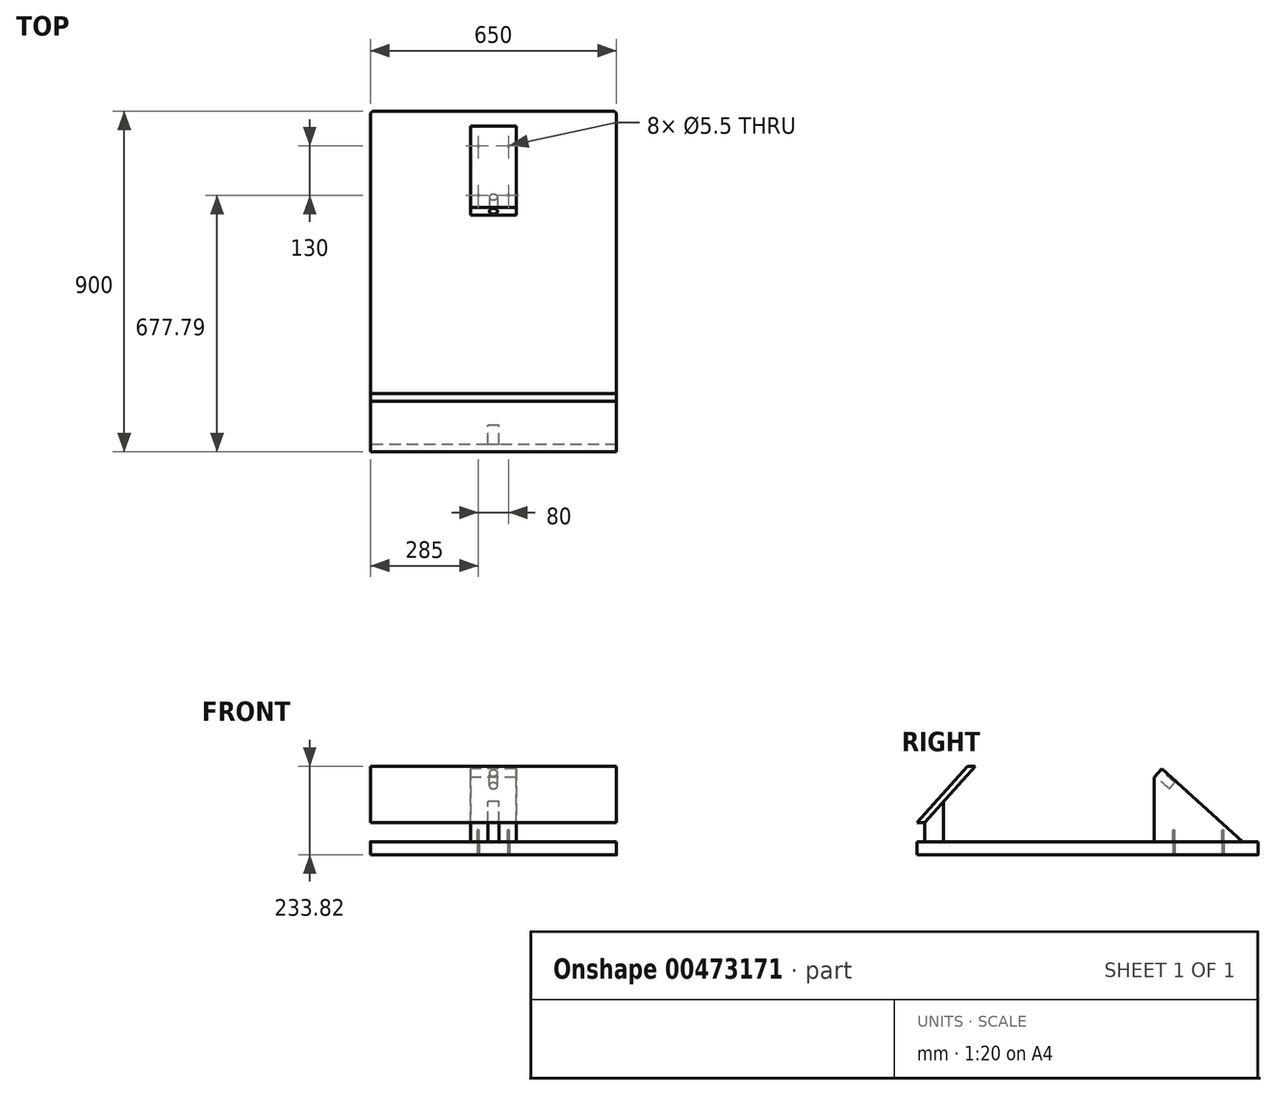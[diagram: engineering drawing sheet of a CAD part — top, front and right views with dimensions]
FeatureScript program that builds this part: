
annotation { "Feature Type Name" : "Feature", "Feature Type Description" : "" }
export const myFeature = defineFeature(function(context is Context, id is Id, definition is map)
    precondition{}
    {
        {
            assignVariable(context, id + "F0", {"name" : "Largeur_Base", "anyValue" : 650});
        }
        {
            assignVariable(context, id + "F1", {"name" : "Bitonio", "anyValue" : 15});
        }
        {
            assignVariable(context, id + "F2", {"name" : "Epaisseur_Arc", "anyValue" : getVariable(context, 'Bitonio') * 2});
        }
        {
            var Q0;
            Q0=qCreatedBy(makeId("Right.planeOp"),FACE);
            var sketch = newSketch(context, id + "F3", { "sketchPlane" : qUnion([Q0])});
            skLineSegment(sketch, "E0.bottom", {"start": v(-655.07, 0) * mm, "end": v(244.93, 0) * mm});
            skLineSegment(sketch, "E0.top", {"start": v(-655.07, 35) * mm, "end": v(244.93, 35) * mm});
            skLineSegment(sketch, "E0.left", {"start": v(-655.07, 0) * mm, "end": v(-655.07, 35) * mm});
            skLineSegment(sketch, "E0.right", {"start": v(244.93, 0) * mm, "end": v(244.93, 35) * mm});
            skLineSegment(sketch, "E1.bottom", {"start": v(-655.07, 35) * mm, "end": v(-635.07, 35) * mm});
            skLineSegment(sketch, "E1.top", {"start": v(-655.07, 85) * mm, "end": v(-635.07, 85) * mm});
            skLineSegment(sketch, "E1.left", {"start": v(-655.07, 35) * mm, "end": v(-655.07, 85) * mm});
            skLineSegment(sketch, "E1.right", {"start": v(-635.07, 35) * mm, "end": v(-635.07, 85) * mm});
            skLineSegment(sketch, "E2", {"start": v(-655.07, 85) * mm, "end": v(-521.46, 233.82) * mm});
            skLineSegment(sketch, "E3", {"start": v(-635.07, 85) * mm, "end": v(-501.46, 233.82) * mm});
            skLineSegment(sketch, "E4", {"start": v(-501.46, 233.82) * mm, "end": v(-521.46, 233.82) * mm});
            skLineSegment(sketch, "E5", {"start": v(-585.07, 35) * mm, "end": v(-585.07, 140.7) * mm});
            skLineSegment(sketch, "E6", {"start": v(-29.36, 35) * mm, "end": v(-29.36, 204.9) * mm});
            skLineSegment(sketch, "E7", {"start": v(-29.36, 204.9) * mm, "end": v(-9.32, 227.23) * mm});
            skLineSegment(sketch, "E8", {"start": v(-9.32, 227.23) * mm, "end": v(204.8, 35) * mm});
            skSolve(sketch);
        }
        {
            var Q0;
            Q0=makeQuery(id+"F3.imprint","IMPRINT",FACE,{"disambiguationData":[TD([[makeQuery(id+"F3.imprint","IMPRINT",EDGE,{"derivedFrom":sQuery(id+"F3.wireOp",EDGE,"E0.bottom")}),1.0]])]});
            var Q1;
            Q1=makeQuery(id+"F3.imprint","IMPRINT",FACE,{"disambiguationData":[TD([[makeQuery(id+"F3.imprint","IMPRINT",EDGE,{"derivedFrom":sQuery(id+"F3.wireOp",EDGE,"E1.bottom")}),1.0]])]});
            var Q2;
            {var subQ1=sQuery(id+"F3.wireOp",EDGE,"E1.top");Q2=makeQuery(id+"F3.imprint","IMPRINT",FACE,{"disambiguationData":[TD([[makeQuery(id+"F3.imprint","IMPRINT",EDGE,{"derivedFrom":subQ1}),1.0]])]});}
            extrude(context, id + "F4", {"entities" : qUnion([Q0, Q1, Q2]), "depth" : (getVariable(context, 'Largeur_Base')) * mm, "offsetDistance" : 25 * mm, "symmetric" : true});
        }
        {
            var Q0;
            Q0=makeQuery(id+"F4.opExtrude","CAP_EDGE",EDGE,{"disambiguationData":[OSD([sQuery(id+"F3.wireOp",EDGE,"E0.left"),sQuery(id+"F3.wireOp",EDGE,"E1.left")])],"isStart":false});
            var Q1;
            Q1=makeQuery(id+"F4.opExtrude","CAP_EDGE",EDGE,{"disambiguationData":[OSD([sQuery(id+"F3.wireOp",EDGE,"E0.right")])],"isStart":false});
            var Q2;
            Q2=makeQuery(id+"F4.opExtrude","CAP_EDGE",EDGE,{"disambiguationData":[OSD([sQuery(id+"F3.wireOp",EDGE,"E0.left"),sQuery(id+"F3.wireOp",EDGE,"E1.left")])],"isStart":true});
            var Q3;
            Q3=makeQuery(id+"F4.opExtrude","CAP_EDGE",EDGE,{"disambiguationData":[OSD([sQuery(id+"F3.wireOp",EDGE,"E0.right")])],"isStart":true});
            fillet(context, id + "F5", {"entities" : qUnion([Q0, Q1, Q2, Q3]), "radius" : 10 * mm, "tangentPropagation" : true, "allowEdgeOverflow" : false});
        }
        {
            var Q0;
            {var subQ0=sQuery(id+"F3.wireOp",EDGE,"E1.right");Q0=makeQuery(id+"F3.imprint","IMPRINT",FACE,{"disambiguationData":[TD([[makeQuery(id+"F3.imprint","IMPRINT",EDGE,{"derivedFrom":subQ0}),-1.0]])]});}
            extrude(context, id + "F6", {"entities" : qUnion([Q0]), "operationType" : NewBodyOperationType.ADD, "depth" : 30 * mm, "offsetDistance" : 25 * mm, "symmetric" : true});
        }
        {
            var Q0;
            {var subQ0=sQuery(id+"F3.wireOp",EDGE,"E6");Q0=makeQuery(id+"F3.imprint","IMPRINT",FACE,{"disambiguationData":[TD([[makeQuery(id+"F3.imprint","IMPRINT",EDGE,{"derivedFrom":subQ0}),-1.0]])]});}
            extrude(context, id + "F7", {"entities" : qUnion([Q0]), "depth" : (getVariable(context, 'Epaisseur_Arc')) * 4 * mm, "offsetDistance" : 25 * mm, "symmetric" : true});
        }
        {
            var Q0;
            Q0=makeQuery(id+"F7.opExtrude","SWEPT_FACE",FACE,{"disambiguationData":[OSD([sQuery(id+"F3.wireOp",EDGE,"E7")])]});
            var sketch = newSketch(context, id + "F8", { "sketchPlane" : qUnion([Q0])});
            skLineSegment(sketch, "E9.bottom", {"start": v(-60, 132.86) * mm, "end": v(60, 132.86) * mm});
            skLineSegment(sketch, "E9.top", {"start": v(-60, 162.86) * mm, "end": v(60, 162.86) * mm});
            skLineSegment(sketch, "E9.left", {"start": v(-60, 132.86) * mm, "end": v(-60, 162.86) * mm});
            skLineSegment(sketch, "E9.right", {"start": v(60, 132.86) * mm, "end": v(60, 162.86) * mm});
            skPoint(sketch, "E9.middle", {"position": v(0, 147.86) * mm});
            skCircle(sketch, "E10", {"center": v(0, 147.86) * mm, "radius": 11 * mm});
            skSolve(sketch);
        }
        {
            var Q0;
            Q0=makeQuery(id+"F8.imprint","IMPRINT",FACE,{"disambiguationData":[TD([[makeQuery(id+"F8.imprint","IMPRINT",EDGE,{"derivedFrom":sQuery(id+"F8.wireOp",EDGE,"E10")}),1.0]])]});
            extrude(context, id + "F9", {"entities" : qUnion([Q0]), "operationType" : NewBodyOperationType.REMOVE, "oppositeDirection" : true, "depth" : 50 * mm, "offsetDistance" : 25 * mm});
        }
        {
            var Q0;
            Q0=makeQuery(id+"F7.opExtrude","SWEPT_FACE",FACE,{"disambiguationData":[OSD([sQuery(id+"F3.wireOp",EDGE,"E0.top")])]});
            var sketch = newSketch(context, id + "F10", { "sketchPlane" : qUnion([Q0])});
            skLineSegment(sketch, "E11", {"start": v(-60, -87.72) * mm, "end": v(60, -87.72) * mm, "construction": true});
            skPoint(sketch, "E12", {"position": v(-40, -22.72) * mm});
            skPoint(sketch, "E13.MirrorP", {"position": v(40, -22.72) * mm});
            skPoint(sketch, "E14.MirrorP", {"position": v(-40, -152.72) * mm});
            skPoint(sketch, "E15.MirrorP", {"position": v(40, -152.72) * mm});
            skSolve(sketch);
        }
        {
            var Q0;
            Q0=sQuery(id+"F10.wireOp",VERTEX,"E12");
            var Q1;
            Q1=sQuery(id+"F10.wireOp",VERTEX,"E13.MirrorP");
            var Q2;
            Q2=sQuery(id+"F10.wireOp",VERTEX,"E15.MirrorP");
            var Q3;
            Q3=sQuery(id+"F10.wireOp",VERTEX,"E14.MirrorP");
            var Q4;
            Q4=makeQuery(id+"F7.opExtrude","SWEPT_BODY",BODY,{"disambiguationData":[OSD([sQuery(id+"F3.wireOp",EDGE,"E0.top"),sQuery(id+"F3.wireOp",EDGE,"E6"),sQuery(id+"F3.wireOp",EDGE,"E7"),sQuery(id+"F3.wireOp",EDGE,"E8")])]});
            hole(context, id + "F11", {"style" : HoleStyle.SIMPLE, "endStyle" : HoleEndStyle.BLIND, "standardTappedOrClearance" : lookupTablePath({ "standard" : "ISO", "fit" : "Normal", "size" : "M5", "type" : "Clearance" }), "standardBlindInLast" : lookupTablePath({ "fit" : "Standard", "standard" : "ISO", "size" : "M5", "type" : "Clearance" }), "holeDiameter" : 5.5 * mm, "majorDiameter" : 5 * mm, "holeDepth" : 30 * mm, "isTappedThrough" : true, "tappedDepth" : 12 * mm, "tapClearance" : 3, "locations" : qUnion([Q0, Q1, Q2, Q3]), "scope" : qUnion([Q4])});
        }
        {
            var Q0;
            Q0=sQuery(id+"F10.wireOp",VERTEX,"E13.MirrorP");
            var Q1;
            Q1=sQuery(id+"F10.wireOp",VERTEX,"E12");
            var Q2;
            Q2=sQuery(id+"F10.wireOp",VERTEX,"E14.MirrorP");
            var Q3;
            Q3=sQuery(id+"F10.wireOp",VERTEX,"E15.MirrorP");
            var Q4;
            Q4=makeQuery(id+"F4.opExtrude","SWEPT_BODY",BODY,{"disambiguationData":[OSD([sQuery(id+"F3.wireOp",EDGE,"E0.bottom"),sQuery(id+"F3.wireOp",EDGE,"E0.top"),sQuery(id+"F3.wireOp",EDGE,"E0.left"),sQuery(id+"F3.wireOp",EDGE,"E0.right"),sQuery(id+"F3.wireOp",EDGE,"E1.left"),sQuery(id+"F3.wireOp",EDGE,"E1.right"),sQuery(id+"F3.wireOp",EDGE,"E2"),sQuery(id+"F3.wireOp",EDGE,"E3"),sQuery(id+"F3.wireOp",EDGE,"E4")])]});
            hole(context, id + "F12", {"style" : HoleStyle.SIMPLE, "endStyle" : HoleEndStyle.THROUGH, "oppositeDirection" : true, "standardTappedOrClearance" : lookupTablePath({ "standard" : "ISO", "fit" : "Normal", "size" : "M5", "type" : "Clearance" }), "standardBlindInLast" : lookupTablePath({ "fit" : "Standard", "standard" : "ISO", "size" : "M5", "type" : "Clearance" }), "holeDiameter" : 5.5 * mm, "majorDiameter" : 5 * mm, "isTappedThrough" : true, "tappedDepth" : 12 * mm, "tapClearance" : 3, "locations" : qUnion([Q0, Q1, Q2, Q3]), "scope" : qUnion([Q4])});
        }
        {
            var Q0;
            Q0=makeQuery(id+"F4.opExtrude","SWEPT_FACE",FACE,{"disambiguationData":[OSD([sQuery(id+"F3.wireOp",EDGE,"E0.top")])]});
            var sketch = newSketch(context, id + "F13", { "sketchPlane" : qUnion([Q0])});
            skLineSegment(sketch, "E16", {"start": v(225, 244.93) * mm, "end": v(225, -255.07) * mm, "construction": true});
            skLineSegment(sketch, "E17", {"start": v(225, -255.07) * mm, "end": v(325, -255.07) * mm, "construction": true});
            skPoint(sketch, "E18", {"position": v(225, -255.07) * mm});
            skSolve(sketch);
        }
    });
